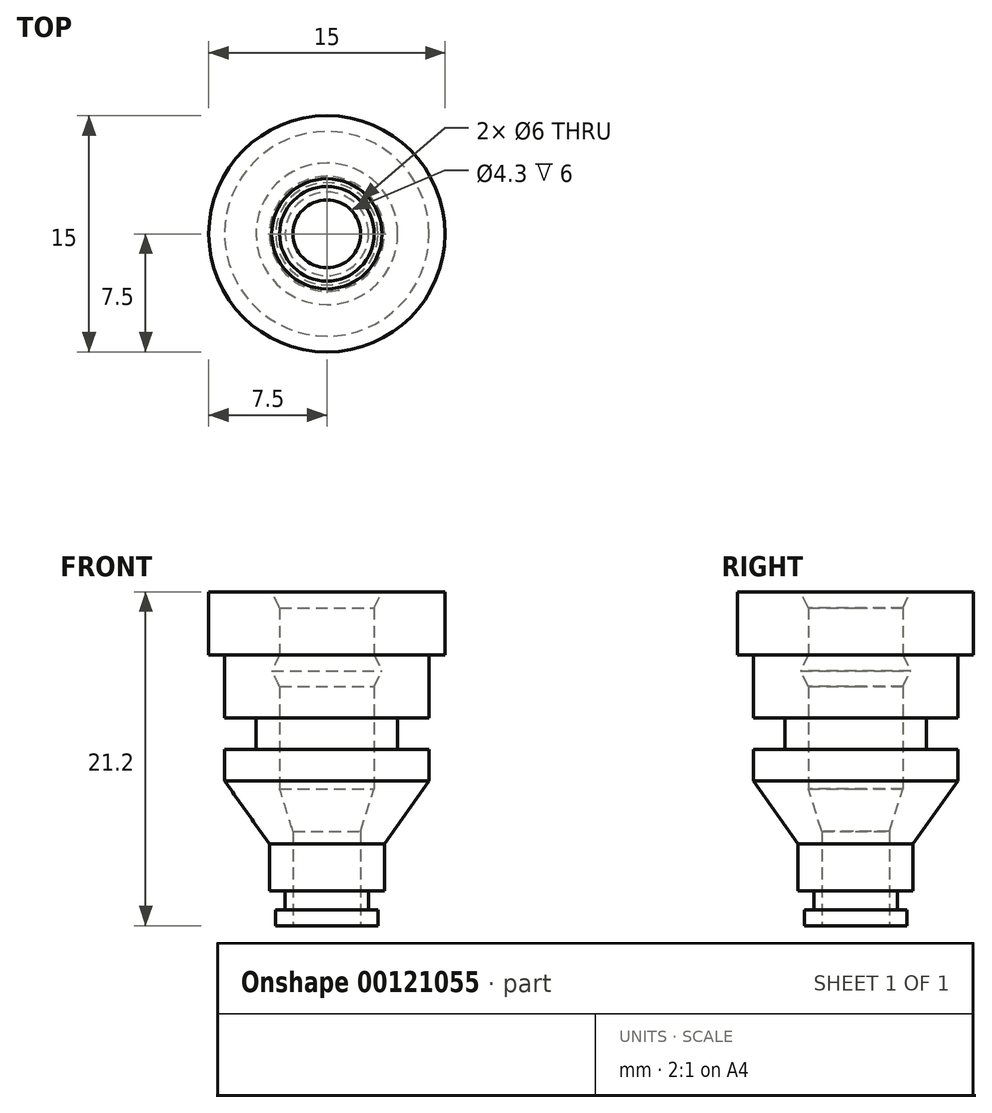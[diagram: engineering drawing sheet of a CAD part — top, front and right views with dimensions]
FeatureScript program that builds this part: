
annotation { "Feature Type Name" : "Feature", "Feature Type Description" : "" }
export const myFeature = defineFeature(function(context is Context, id is Id, definition is map)
    precondition{}
    {
        {
            var Q0;
            Q0=qCreatedBy(makeId("Right.planeOp"),FACE);
            var sketch = newSketch(context, id + "F0", { "sketchPlane" : qUnion([Q0])});
            skLineSegment(sketch, "E0", {"start": v(0, 0) * mm, "end": v(2.15, 0) * mm, "construction": true});
            skLineSegment(sketch, "E1", {"start": v(2.15, 0) * mm, "end": v(2.15, 6) * mm});
            skLineSegment(sketch, "E2", {"start": v(2.15, 6) * mm, "end": v(3, 8.7) * mm});
            skLineSegment(sketch, "E3", {"start": v(3, 8.7) * mm, "end": v(0, 8.7) * mm, "construction": true});
            skLineSegment(sketch, "E4", {"start": v(3, 8.7) * mm, "end": v(3, 15.2) * mm});
            skLineSegment(sketch, "E5", {"start": v(3, 15.2) * mm, "end": v(3.5, 16.2) * mm});
            skLineSegment(sketch, "E6", {"start": v(3.5, 16.2) * mm, "end": v(0, 16.2) * mm, "construction": true});
            skLineSegment(sketch, "E7", {"start": v(3.5, 16.2) * mm, "end": v(3, 17.2) * mm});
            skLineSegment(sketch, "E8", {"start": v(3, 17.2) * mm, "end": v(0, 17.2) * mm, "construction": true});
            skLineSegment(sketch, "E9", {"start": v(3, 17.2) * mm, "end": v(3, 20.2) * mm});
            skLineSegment(sketch, "E10", {"start": v(3, 20.2) * mm, "end": v(3.5, 21.2) * mm});
            skLineSegment(sketch, "E11", {"start": v(3.5, 21.2) * mm, "end": v(0, 21.2) * mm, "construction": true});
            skLineSegment(sketch, "E12", {"start": v(3.5, 21.2) * mm, "end": v(7.5, 21.2) * mm});
            skLineSegment(sketch, "E13", {"start": v(7.5, 21.2) * mm, "end": v(7.5, 17.2) * mm});
            skLineSegment(sketch, "E14", {"start": v(7.5, 17.2) * mm, "end": v(6.5, 17.2) * mm});
            skLineSegment(sketch, "E15", {"start": v(6.5, 17.2) * mm, "end": v(6.5, 13.2) * mm});
            skLineSegment(sketch, "E16", {"start": v(6.5, 13.2) * mm, "end": v(4.5, 13.2) * mm});
            skLineSegment(sketch, "E17", {"start": v(4.5, 13.2) * mm, "end": v(4.5, 11.2) * mm});
            skLineSegment(sketch, "E18", {"start": v(4.5, 11.2) * mm, "end": v(6.5, 11.2) * mm});
            skLineSegment(sketch, "E19", {"start": v(6.5, 11.2) * mm, "end": v(6.5, 9.2) * mm});
            skLineSegment(sketch, "E20", {"start": v(2.15, 0) * mm, "end": v(3.25, 0) * mm});
            skLineSegment(sketch, "E21", {"start": v(3.25, 1) * mm, "end": v(2.65, 1) * mm});
            skLineSegment(sketch, "E22", {"start": v(2.65, 1) * mm, "end": v(2.65, 2.2) * mm});
            skLineSegment(sketch, "E23", {"start": v(2.65, 2.2) * mm, "end": v(3.65, 2.2) * mm});
            skLineSegment(sketch, "E24", {"start": v(3.65, 2.2) * mm, "end": v(3.65, 5.2) * mm});
            skLineSegment(sketch, "E25", {"start": v(3.65, 5.2) * mm, "end": v(6.5, 9.2) * mm});
            skLineSegment(sketch, "E26", {"start": v(0, 0) * mm, "end": v(0, 4.27) * mm});
            skLineSegment(sketch, "E27", {"start": v(3.25, 1) * mm, "end": v(3.25, 0) * mm});
            skSolve(sketch);
        }
        {
            var Q0;
            Q0=makeQuery(id+"F0.imprint","IMPRINT",FACE,{"disambiguationData":[TD([[makeQuery(id+"F0.imprint","IMPRINT",EDGE,{"derivedFrom":sQuery(id+"F0.wireOp",EDGE,"E1")}),-1.0]])]});
            var Q1;
            Q1=sQuery(id+"F0.wireOp",EDGE,"E26");
            revolve(context, id + "F1", {"entities" : qUnion([Q0]), "axis" : qUnion([Q1]), "revolveType" : RevolveType.FULL});
        }
    });
